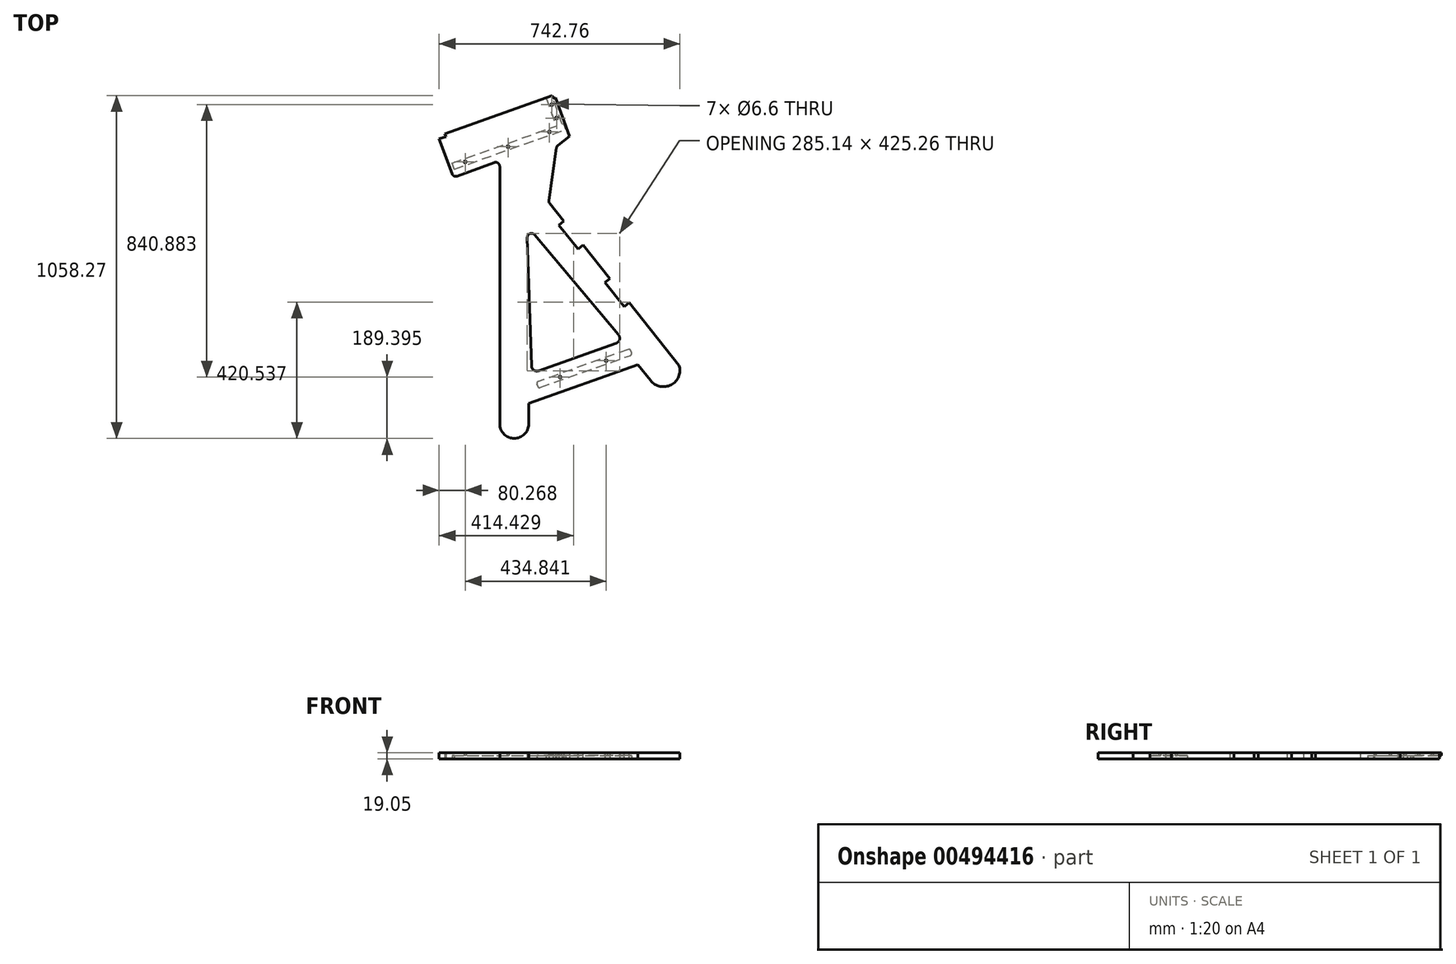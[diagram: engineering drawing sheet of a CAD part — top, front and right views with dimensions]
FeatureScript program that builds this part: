
annotation { "Feature Type Name" : "Feature", "Feature Type Description" : "" }
export const myFeature = defineFeature(function(context is Context, id is Id, definition is map)
    precondition{}
    {
        {
            var Q0;
            Q0=qCreatedBy(makeId("Top.planeOp"),FACE);
            var sketch = newSketch(context, id + "F0", { "sketchPlane" : qUnion([Q0])});
            skLineSegment(sketch, "E0", {"start": v(-306.62, -10.3) * mm, "end": v(-306.88, -10.27) * mm});
            skLineSegment(sketch, "E1", {"start": v(727.27, -283.58) * mm, "end": v(727.27, 427.9) * mm});
            skPoint(sketch, "E2.visualSharp", {"position": v(727.27, -334.1) * mm});
            skPoint(sketch, "E3.visualSharp", {"position": v(828.87, -334.66) * mm});
            skLineSegment(sketch, "E4", {"start": v(902.24, 568.5) * mm, "end": v(878.6, 406.65) * mm});
            skLineSegment(sketch, "E5", {"start": v(727.27, 427.9) * mm, "end": v(727.27, 511.3) * mm});
            skLineSegment(sketch, "E6", {"start": v(710.18, 523.22) * mm, "end": v(596.17, 481.24) * mm});
            skLineSegment(sketch, "E7", {"start": v(579.86, 488.77) * mm, "end": v(540.37, 596.03) * mm});
            skLineSegment(sketch, "E8", {"start": v(540.37, 596.03) * mm, "end": v(561.03, 603.39) * mm});
            skLineSegment(sketch, "E9", {"start": v(899.3, 723.83) * mm, "end": v(941.9, 604.19) * mm});
            skLineSegment(sketch, "E10", {"start": v(906.95, 576.64) * mm, "end": v(941.9, 604.19) * mm});
            skLineSegment(sketch, "E11", {"start": v(540.37, 596.03) * mm, "end": v(561.03, 603.39) * mm, "construction": true});
            skPoint(sketch, "E12.visualSharp", {"position": v(1175.92, -180.14) * mm});
            skLineSegment(sketch, "E13", {"start": v(825.1, -104.38) * mm, "end": v(812.23, 291.9) * mm});
            skLineSegment(sketch, "E14", {"start": v(834.65, 300.48) * mm, "end": v(1093.51, -8.04) * mm});
            skPoint(sketch, "E15.visualSharp", {"position": v(811.04, 328.62) * mm});
            skArc(sketch, "E15.filletArc", {"start": v(834.65, 300.48) * mm, "mid": v(820.38, 304.18) * mm, "end": v(812.23, 291.9) * mm});
            skLineSegment(sketch, "E16", {"start": v(584.25, 476.85) * mm, "end": v(941.9, 604.19) * mm, "construction": true});
            skLineSegment(sketch, "E17", {"start": v(573.37, 506.42) * mm, "end": v(591.31, 512.8) * mm, "construction": true});
            skLineSegment(sketch, "E18", {"start": v(881.25, 396.88) * mm, "end": v(1280.84, -102.55) * mm});
            skLineSegment(sketch, "E19", {"start": v(1185.54, -137.77) * mm, "end": v(1280.84, -102.55) * mm, "construction": true});
            skArc(sketch, "E20", {"start": v(1192.54, -149.45) * mm, "mid": v(1256.13, -162.6) * mm, "end": v(1280.84, -102.55) * mm});
            skLineSegment(sketch, "E21", {"start": v(816.46, -283.58) * mm, "end": v(816.46, -220.06) * mm});
            skLineSegment(sketch, "E22", {"start": v(923.23, 732.35) * mm, "end": v(1268.85, -238.36) * mm, "construction": true});
            skPoint(sketch, "E23.visualSharp", {"position": v(1185.54, -137.77) * mm});
            skPoint(sketch, "E24.visualSharp", {"position": v(877.8, 401.2) * mm});
            skArc(sketch, "E24.filletArc", {"start": v(878.6, 406.65) * mm, "mid": v(878.9, 401.5) * mm, "end": v(881.25, 396.88) * mm});
            skPoint(sketch, "E25.visualSharp", {"position": v(902.97, 573.5) * mm});
            skArc(sketch, "E25.filletArc", {"start": v(906.95, 576.64) * mm, "mid": v(903.81, 573.02) * mm, "end": v(902.24, 568.5) * mm});
            skArc(sketch, "E26.filletArc", {"start": v(727.27, 511.3) * mm, "mid": v(721.83, 521.72) * mm, "end": v(710.18, 523.22) * mm});
            skLineSegment(sketch, "E27", {"start": v(557.84, 612.36) * mm, "end": v(888.53, 730.1) * mm});
            skLineSegment(sketch, "E28", {"start": v(557.84, 612.36) * mm, "end": v(561.03, 603.39) * mm});
            skLineSegment(sketch, "E29", {"start": v(888.53, 730.1) * mm, "end": v(891.73, 721.13) * mm});
            skLineSegment(sketch, "E30.trimOffspring", {"start": v(891.73, 721.13) * mm, "end": v(899.3, 723.83) * mm, "construction": true});
            skLineSegment(sketch, "E31.trimOffspring", {"start": v(891.73, 721.13) * mm, "end": v(899.3, 723.83) * mm});
            skLineSegment(sketch, "E32", {"start": v(540.37, 596.03) * mm, "end": v(913.6, -417.7) * mm, "construction": true});
            skLineSegment(sketch, "E33", {"start": v(877.85, -320.58) * mm, "end": v(1232.27, -194.4) * mm, "construction": true});
            skLineSegment(sketch, "E34", {"start": v(816.46, -220.06) * mm, "end": v(1153.13, -100.19) * mm});
            skLineSegment(sketch, "E35", {"start": v(847.13, -119.4) * mm, "end": v(1086.4, -34.2) * mm});
            skArc(sketch, "E36", {"start": v(727.27, -283.58) * mm, "mid": v(771.86, -328.17) * mm, "end": v(816.46, -283.58) * mm});
            skPoint(sketch, "E37.visualSharp", {"position": v(584.25, 476.85) * mm});
            skArc(sketch, "E37.filletArc", {"start": v(579.86, 488.77) * mm, "mid": v(586.46, 481.63) * mm, "end": v(596.17, 481.24) * mm});
            skPoint(sketch, "E38.visualSharp", {"position": v(1108.78, -26.24) * mm});
            skArc(sketch, "E38.filletArc", {"start": v(1086.4, -34.2) * mm, "mid": v(1096.8, -22.98) * mm, "end": v(1093.51, -8.04) * mm});
            skPoint(sketch, "E39.visualSharp", {"position": v(825.83, -126.99) * mm});
            skArc(sketch, "E39.filletArc", {"start": v(825.1, -104.38) * mm, "mid": v(832.3, -117.5) * mm, "end": v(847.13, -119.4) * mm});
            skLineSegment(sketch, "E40", {"start": v(1153.13, -100.19) * mm, "end": v(1192.54, -149.45) * mm});
            skPoint(sketch, "E41", {"position": v(1256.13, -162.6) * mm});
            skSolve(sketch);
        }
        {
            var Q0;
            Q0=makeQuery(id+"F0.imprint","IMPRINT",FACE,{"disambiguationData":[TD([[makeQuery(id+"F0.imprint","IMPRINT",EDGE,{"derivedFrom":sQuery(id+"F0.wireOp",EDGE,"oAVC5DI8-kh1G-Qbfy-uwvq-Txyh6lFHP0Ui")}),1.0]])]});
            var Q1;
            Q1=makeQuery(id+"F0.imprint","IMPRINT",FACE,{"disambiguationData":[TD([[makeQuery(id+"F0.imprint","IMPRINT",EDGE,{"derivedFrom":sQuery(id+"F0.wireOp",EDGE,"E1")}),-1.0]])]});
            extrude(context, id + "F1", {"entities" : qUnion([Q0, Q1]), "depth" : 19.05 * mm});
        }
        {
            var Q0;
            {var subQ2=sQuery(id+"F0.wireOp",EDGE,"E1");Q0=makeQuery(id+"F0.imprint","IMPRINT",FACE,{"disambiguationData":[TD([[makeQuery(id+"F0.imprint","IMPRINT",EDGE,{"derivedFrom":subQ2}),-1.0]])]});}
            var sketch = newSketch(context, id + "F2", { "sketchPlane" : qUnion([Q0])});
            skLineSegment(sketch, "E42", {"start": v(852.3, -170.94) * mm, "end": v(1129.86, -72.11) * mm});
            skLineSegment(sketch, "E43", {"start": v(1123.5, -53.62) * mm, "end": v(845.93, -152.44) * mm});
            skLineSegment(sketch, "E44", {"start": v(1133.77, -64.18) * mm, "end": v(1131.67, -57.65) * mm});
            skLineSegment(sketch, "E45", {"start": v(844.12, -166.9) * mm, "end": v(842.02, -160.38) * mm});
            skPoint(sketch, "E46.visualSharp", {"position": v(846.13, -173.13) * mm});
            skArc(sketch, "E46.filletArc", {"start": v(844.12, -166.9) * mm, "mid": v(847.36, -170.65) * mm, "end": v(852.3, -170.94) * mm});
            skPoint(sketch, "E47.visualSharp", {"position": v(840.12, -154.51) * mm});
            skArc(sketch, "E47.filletArc", {"start": v(845.93, -152.44) * mm, "mid": v(842.36, -155.62) * mm, "end": v(842.02, -160.38) * mm});
            skPoint(sketch, "E48.visualSharp", {"position": v(1135.67, -70.04) * mm});
            skArc(sketch, "E48.filletArc", {"start": v(1129.86, -72.11) * mm, "mid": v(1133.43, -68.94) * mm, "end": v(1133.77, -64.18) * mm});
            skPoint(sketch, "E49.visualSharp", {"position": v(1129.66, -51.42) * mm});
            skArc(sketch, "E49.filletArc", {"start": v(1131.67, -57.65) * mm, "mid": v(1128.43, -53.9) * mm, "end": v(1123.5, -53.62) * mm});
            skSolve(sketch);
        }
        {
            var Q0;
            Q0=qSketchRegion(id+"F2",true);
            extrude(context, id + "F3", {"entities" : qUnion([Q0]), "operationType" : NewBodyOperationType.REMOVE, "depth" : 9.52 * mm});
        }
        {
            var Q0;
            {var subQ2=sQuery(id+"F0.wireOp",EDGE,"E1");Q0=makeQuery(id+"F0.imprint","IMPRINT",FACE,{"disambiguationData":[TD([[makeQuery(id+"F0.imprint","IMPRINT",EDGE,{"derivedFrom":subQ2}),-1.0]])]});}
            var sketch = newSketch(context, id + "F4", { "sketchPlane" : qUnion([Q0])});
            skLineSegment(sketch, "E50.bottom", {"start": v(586.5, 502.94) * mm, "end": v(930.54, 625.43) * mm});
            skLineSegment(sketch, "E50.top", {"start": v(579.94, 521.37) * mm, "end": v(901.35, 635.8) * mm});
            skLineSegment(sketch, "E50.left", {"start": v(586.5, 502.94) * mm, "end": v(579.94, 521.37) * mm});
            skLineSegment(sketch, "E51", {"start": v(870.05, 723.7) * mm, "end": v(901.35, 635.8) * mm});
            skPoint(sketch, "E52.0", {"position": v(891.73, 721.13) * mm});
            skPoint(sketch, "E53.0", {"position": v(888.53, 730.1) * mm});
            skLineSegment(sketch, "E54", {"start": v(888.53, 730.1) * mm, "end": v(891.73, 721.13) * mm});
            skLineSegment(sketch, "E55", {"start": v(888.53, 730.1) * mm, "end": v(870.05, 723.7) * mm});
            skLineSegment(sketch, "E56", {"start": v(919.83, 642.19) * mm, "end": v(891.73, 721.13) * mm});
            skLineSegment(sketch, "E57", {"start": v(919.83, 642.19) * mm, "end": v(924.04, 643.68) * mm});
            skLineSegment(sketch, "E58", {"start": v(930.54, 625.43) * mm, "end": v(924.04, 643.68) * mm});
            skSolve(sketch);
        }
        {
            var Q0;
            Q0=qSketchRegion(id+"F4",true);
            extrude(context, id + "F5", {"entities" : qUnion([Q0]), "operationType" : NewBodyOperationType.REMOVE, "depth" : 9.52 * mm});
        }
        {
            var Q0;
            Q0=makeQuery(id+"F1.opExtrude","SWEPT_FACE",FACE,{"disambiguationData":[OSD([sQuery(id+"F0.wireOp",EDGE,"E18")])]});
            var sketch = newSketch(context, id + "F6", { "sketchPlane" : qUnion([Q0])});
            skLineSegment(sketch, "E59", {"start": v(-310.5, 19.05) * mm, "end": v(-310.5, 0) * mm});
            skLineSegment(sketch, "E60", {"start": v(-310.5, 0) * mm, "end": v(-405.25, 0) * mm});
            skLineSegment(sketch, "E61", {"start": v(-405.25, 0) * mm, "end": v(-405.25, 19.05) * mm});
            skLineSegment(sketch, "E62", {"start": v(-405.25, 19.05) * mm, "end": v(-310.5, 19.05) * mm});
            skLineSegment(sketch, "E63", {"start": v(-537.62, 21.33) * mm, "end": v(-537.62, -0.7) * mm});
            skLineSegment(sketch, "E64", {"start": v(-537.62, -0.7) * mm, "end": v(-632.36, -0.7) * mm});
            skLineSegment(sketch, "E65", {"start": v(-632.36, -0.7) * mm, "end": v(-632.36, 21.33) * mm});
            skLineSegment(sketch, "E66", {"start": v(-632.36, 21.33) * mm, "end": v(-537.62, 21.33) * mm});
            skSolve(sketch);
        }
        {
            var Q0;
            Q0=qSketchRegion(id+"F6",true);
            extrude(context, id + "F7", {"entities" : qUnion([Q0]), "operationType" : NewBodyOperationType.REMOVE, "oppositeDirection" : true, "depth" : 19.56 * mm});
        }
        {
            var Q0;
            Q0=makeQuery(id+"F0.imprint","IMPRINT",FACE,{"disambiguationData":[TD([[makeQuery(id+"F0.imprint","IMPRINT",EDGE,{"derivedFrom":sQuery(id+"F0.wireOp",EDGE,"E1")}),-1.0]])]});
            var sketch = newSketch(context, id + "F8", { "sketchPlane" : qUnion([Q0])});
            skLineSegment(sketch, "E67", {"start": v(916.91, 620.58) * mm, "end": v(879.28, 726.3) * mm, "construction": true});
            skLineSegment(sketch, "E68.0", {"start": v(919.83, 642.19) * mm, "end": v(891.73, 721.13) * mm});
            skCircle(sketch, "E69", {"center": v(902.66, 660.61) * mm, "radius": 3.3 * mm});
            skCircle(sketch, "E70", {"center": v(887.92, 702.1) * mm, "radius": 3.3 * mm});
            skLineSegment(sketch, "E71", {"start": v(921.57, 632.52) * mm, "end": v(583.89, 512.3) * mm, "construction": true});
            skCircle(sketch, "E72", {"center": v(880.54, 617.91) * mm, "radius": 3.3 * mm});
            skCircle(sketch, "E73", {"center": v(620.64, 525.38) * mm, "radius": 3.3 * mm});
            skCircle(sketch, "E74", {"center": v(752.73, 572.4) * mm, "radius": 3.3 * mm});
            skLineSegment(sketch, "E75.0", {"start": v(1133.77, -64.18) * mm, "end": v(1131.67, -57.65) * mm});
            skLineSegment(sketch, "E76.0", {"start": v(1123.5, -53.62) * mm, "end": v(845.93, -152.44) * mm});
            skLineSegment(sketch, "E77", {"start": v(1123.33, -64.1) * mm, "end": v(843.4, -163.77) * mm, "construction": true});
            skCircle(sketch, "E78", {"center": v(1055.48, -88.26) * mm, "radius": 3.3 * mm});
            skCircle(sketch, "E79", {"center": v(913.6, -138.78) * mm, "radius": 3.3 * mm});
            skLineSegment(sketch, "E80", {"start": v(752.73, 572.4) * mm, "end": v(620.64, 525.38) * mm});
            skSolve(sketch);
        }
        {
            var Q0;
            Q0=qSketchRegion(id+"F8",true);
            extrude(context, id + "F9", {"entities" : qUnion([Q0]), "operationType" : NewBodyOperationType.REMOVE, "endBound" : BoundingType.THROUGH_ALL, "depth" : 25.4 * mm});
        }
    });
